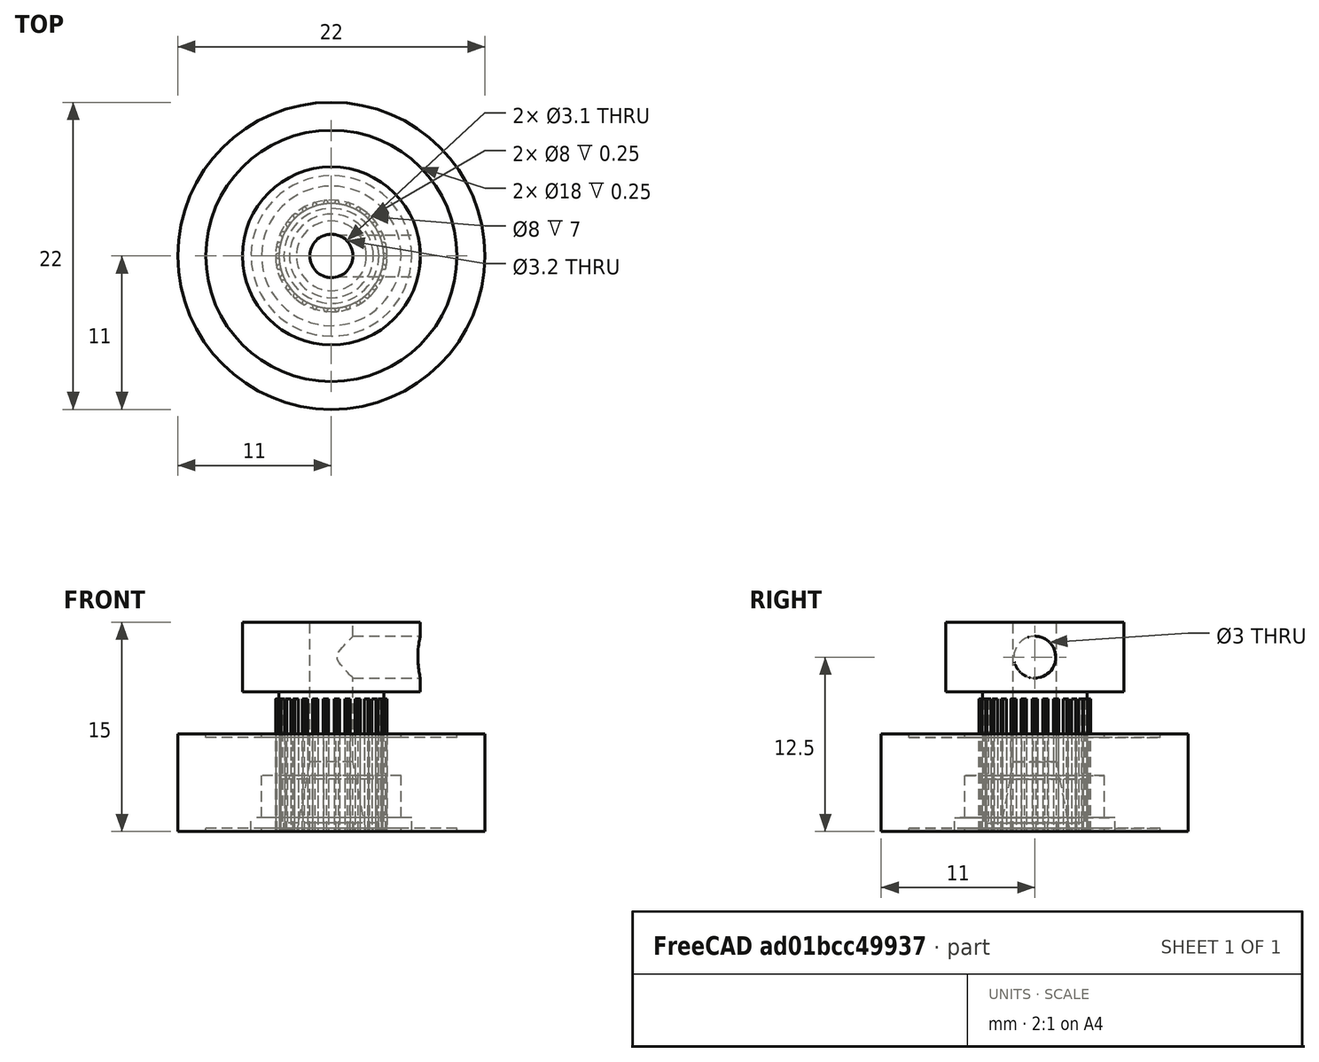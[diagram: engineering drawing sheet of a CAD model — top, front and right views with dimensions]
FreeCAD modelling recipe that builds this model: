
FCSTD DOCUMENT  (FreeCAD 0.14R3700 (Git))
Label: F623ZZ
License: CC-BY 3.0
LicenseURL: http://creativecommons.org/licenses/by/3.0/
objects: Part::Cylinder×19, Part::Cut×14, Part::MultiFuse×2, Part::Cone×1, Part::Part2DObjectPython×1, PartDesign::Pad×1
note: 39 computed .brp shape members not serialized (recipe doc carries the construction recipe); baked Part::Feature solids carry a one-line shape summary decoded from their .brp

FEATURE [Part::Cylinder] Cylinder  label="Base"
  Angle = 360
  Height = 4
  Radius = 5
FEATURE [Part::Cylinder] Cylinder001  label="Flang"
  Angle = 360
  Height = 1
  Radius = 5.75
FEATURE [Part::Cylinder] Cylinder002
  Angle = 360
  Height = 0.5
  Radius = 3
FEATURE [Part::Cylinder] Cylinder003
  Angle = 360
  Height = 0.25
  Radius = 4
FEATURE [Part::Cylinder] Cylinder004  label="M3"
  Angle = 360
  Height = 4
  Radius = 1.55
FEATURE [Part::Cut] Cut  label="Groove"
  Base = -> Cylinder003
  Tool = -> Cylinder002
FEATURE [Part::Cylinder] Cylinder005
  Angle = 360
  Height = 0.5
  Radius = 3
FEATURE [Part::Cylinder] Cylinder006
  Angle = 360
  Height = 0.25
  Radius = 4
FEATURE [Part::Cut] Cut001  label="Groove001"
  Base = -> Cylinder006
  Placement = pos=(0,0,3.75) rot=(0,0,1;0rad)
  Tool = -> Cylinder005
FEATURE [Part::Cut] Cut002
  Base = -> Cylinder
  Tool = -> Cut001
FEATURE [Part::MultiFuse] Fusion
  Shapes = -> [Cut002,Cylinder001]
FEATURE [Part::Cut] Cut003
  Base = -> Fusion
  Tool = -> Cut
FEATURE [Part::Cut] Cut004  label="F623ZZ"
  Base = -> Cut003
  Tool = -> Cylinder004
FEATURE [Part::Cylinder] Cylinder007  label="Cylinder"
  Angle = 360
  Height = 15
  Radius = 3.75
FEATURE [Part::Cylinder] Cylinder008  label="Cylinder007"
  Angle = 360
  Height = 5
  Placement = pos=(0,0,10) rot=(0,0,1;0rad)
  Radius = 6.375
FEATURE [Part::Cylinder] Cylinder009  label="M3-1"
  Angle = 360
  Height = 15
  Radius = 1.55
FEATURE [Part::Cylinder] Cylinder010  label="M3-2"
  Angle = 360
  Height = 7
  Placement = pos=(0,0,12.5) rot=(0,1,0;1.5708rad)
  Radius = 1.5
FEATURE [Part::Cone] Cone  label="ConeTop"
  Angle = 360
  Height = 5
  Radius1 = 2.5
  Radius2 = 1.55
FEATURE [Part::Part2DObjectPython] InvoluteGear  # Draft 2D object (typed FeaturePython)
  Modules = 0.25
  NumberOfCurves = 0
  NumberOfTeeth = 30
  PressureAngle = 20
FEATURE [PartDesign::Pad] Pad
  Length = 9.5
  Length2 = 100
  Sketch = -> InvoluteGear
  Type = 0
FEATURE [Part::MultiFuse] Fusion001
  Shapes = -> [Cylinder007,Cylinder008,Pad]
FEATURE [Part::Cut] Cut005
  Base = -> Fusion001
  Tool = -> Cone
FEATURE [Part::Cut] Cut006
  Base = -> Cut005
  Tool = -> Cylinder010
FEATURE [Part::Cut] Cut007  label="ExtruderGear"
  Base = -> Cut006
  Tool = -> Cylinder009
FEATURE [Part::Cylinder] Cylinder011  label="Cylinder008"
  Angle = 360
  Height = 7
  Radius = 4
FEATURE [Part::Cylinder] Cylinder012  label="Cylinder009"
  Angle = 360
  Height = 7
  Radius = 11
FEATURE [Part::Cylinder] Cylinder013  label="Cylinder010"
  Angle = 360
  Height = 0.25
  Radius = 5
FEATURE [Part::Cylinder] Cylinder014  label="Cylinder011"
  Angle = 360
  Height = 0.25
  Radius = 9
FEATURE [Part::Cut] Cut008  label="Groove002"
  Base = -> Cylinder014
  Tool = -> Cylinder013
FEATURE [Part::Cut] Cut009
  Base = -> Cylinder012
  Tool = -> Cylinder011
FEATURE [Part::Cylinder] Cylinder015  label="Cylinder017"
  Angle = 360
  Height = 0.25
  Radius = 5
FEATURE [Part::Cylinder] Cylinder016  label="Cylinder018"
  Angle = 360
  Height = 0.25
  Radius = 9
FEATURE [Part::Cut] Cut010  label="Groove003"
  Base = -> Cylinder016
  Placement = pos=(0,0,6.75) rot=(0,0,1;0rad)
  Tool = -> Cylinder015
FEATURE [Part::Cut] Cut011
  Base = -> Cut009
  Tool = -> Cut010
FEATURE [Part::Cut] Cut012  label="ILQ-9"
  Base = -> Cut011
  Tool = -> Cut008
FEATURE [Part::Cylinder] Cylinder017  label="Cylinder019"
  Angle = 360
  Height = 0.6
  Radius = 3.4
FEATURE [Part::Cylinder] Cylinder018  label="Cylinder020"
  Angle = 360
  Height = 0.6
  Radius = 1.6
FEATURE [Part::Cut] Cut013  label="M3-Washer"
  Base = -> Cylinder017
  Tool = -> Cylinder018
